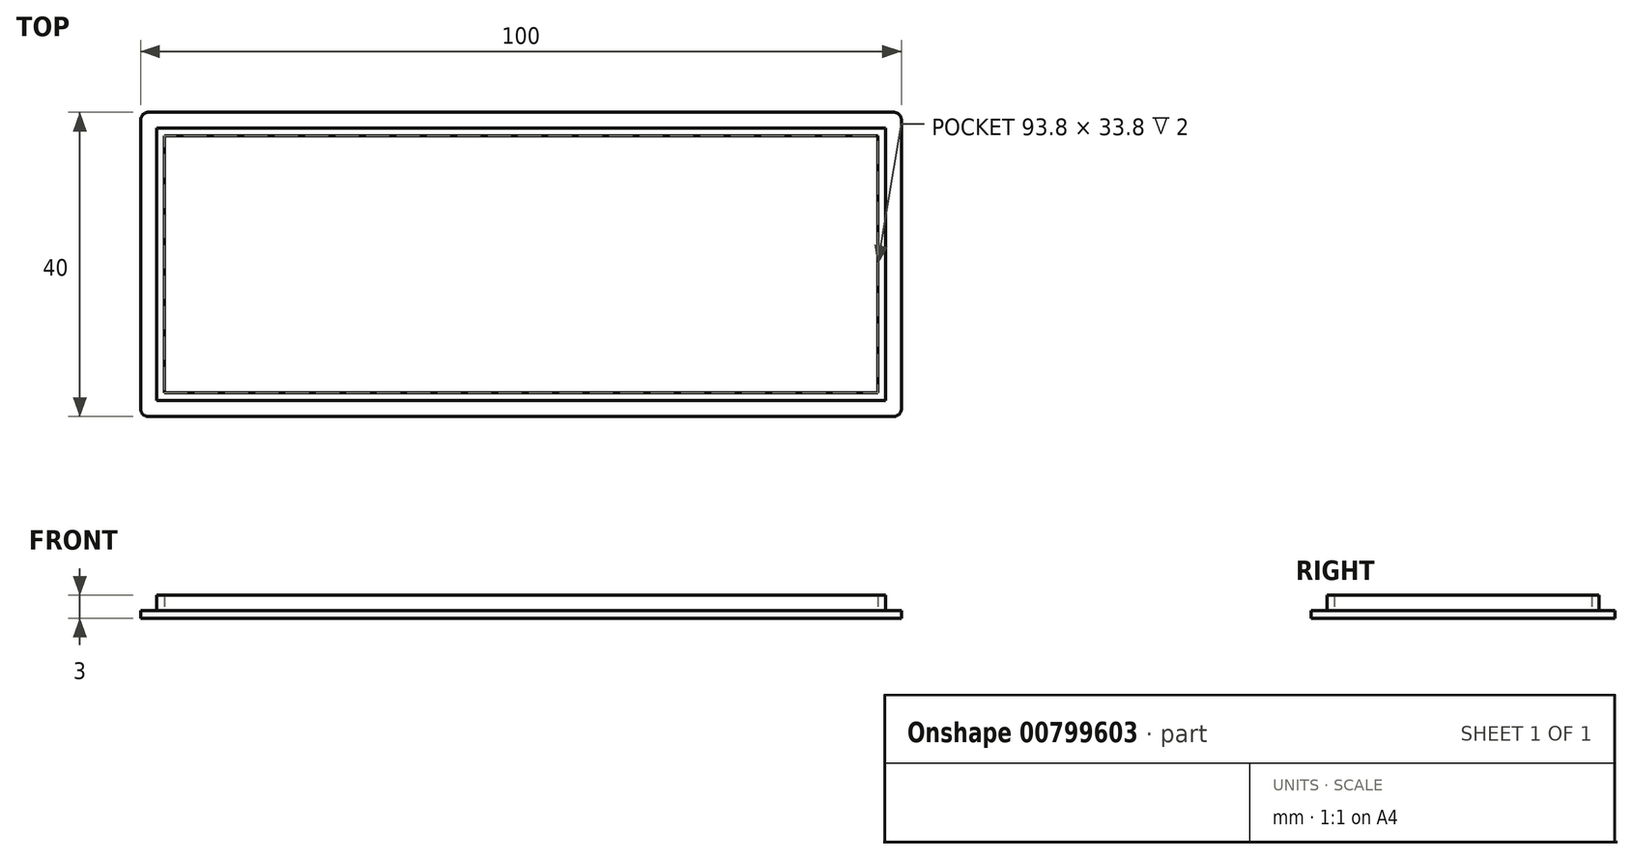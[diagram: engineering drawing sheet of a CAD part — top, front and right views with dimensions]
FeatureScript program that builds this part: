
annotation { "Feature Type Name" : "Feature", "Feature Type Description" : "" }
export const myFeature = defineFeature(function(context is Context, id is Id, definition is map)
    precondition{}
    {
        {
            var Q0;
            Q0=qCreatedBy(makeId("Top.planeOp"),FACE);
            var sketch = newSketch(context, id + "F0", { "sketchPlane" : qUnion([Q0])});
            skLineSegment(sketch, "E0.bottom", {"start": v(0, 0) * mm, "end": v(100, 0) * mm});
            skLineSegment(sketch, "E0.top", {"start": v(0, 40) * mm, "end": v(100, 40) * mm});
            skLineSegment(sketch, "E0.left", {"start": v(0, 0) * mm, "end": v(0, 40) * mm});
            skLineSegment(sketch, "E0.right", {"start": v(100, 0) * mm, "end": v(100, 40) * mm});
            skSolve(sketch);
        }
        {
            var Q0;
            Q0=makeQuery(id+"F0.imprint","IMPRINT",FACE,{"disambiguationData":[TD([[makeQuery(id+"F0.imprint","IMPRINT",EDGE,{"derivedFrom":sQuery(id+"F0.wireOp",EDGE,"E0.bottom")}),1.0]])]});
            extrude(context, id + "F1", {"entities" : qUnion([Q0]), "depth" : 1 * mm, "offsetDistance" : 25 * mm});
        }
        {
            var Q0;
            Q0=makeQuery(id+"F1.opExtrude","CAP_FACE",FACE,{"disambiguationData":[OSD([sQuery(id+"F0.wireOp",EDGE,"E0.bottom"),sQuery(id+"F0.wireOp",EDGE,"E0.top"),sQuery(id+"F0.wireOp",EDGE,"E0.left"),sQuery(id+"F0.wireOp",EDGE,"E0.right")])],"isStart":false});
            var sketch = newSketch(context, id + "F2", { "sketchPlane" : qUnion([Q0])});
            skLineSegment(sketch, "E1.bottom", {"start": v(2.1, 37.9) * mm, "end": v(97.9, 37.9) * mm});
            skLineSegment(sketch, "E1.top", {"start": v(2.1, 2.1) * mm, "end": v(97.9, 2.1) * mm});
            skLineSegment(sketch, "E1.left", {"start": v(2.1, 37.9) * mm, "end": v(2.1, 2.1) * mm});
            skLineSegment(sketch, "E1.right", {"start": v(97.9, 37.9) * mm, "end": v(97.9, 2.1) * mm});
            skLineSegment(sketch, "E2.bottom", {"start": v(3.1, 36.9) * mm, "end": v(96.9, 36.9) * mm});
            skLineSegment(sketch, "E2.top", {"start": v(3.1, 3.1) * mm, "end": v(96.9, 3.1) * mm});
            skLineSegment(sketch, "E2.left", {"start": v(3.1, 36.9) * mm, "end": v(3.1, 3.1) * mm});
            skLineSegment(sketch, "E2.right", {"start": v(96.9, 36.9) * mm, "end": v(96.9, 3.1) * mm});
            skSolve(sketch);
        }
        {
            var Q0;
            Q0=makeQuery(id+"F2.imprint","IMPRINT",FACE,{"disambiguationData":[TD([[makeQuery(id+"F2.imprint","IMPRINT",EDGE,{"derivedFrom":sQuery(id+"F2.wireOp",EDGE,"E1.bottom")}),-1.0]])]});
            extrude(context, id + "F3", {"entities" : qUnion([Q0]), "operationType" : NewBodyOperationType.ADD, "depth" : 2 * mm, "offsetDistance" : 25 * mm});
        }
        {
            var Q0;
            Q0=makeQuery(id+"F1.opExtrude","SWEPT_EDGE",EDGE,{"disambiguationData":[OSD([sQuery(id+"F0.wireOp",EDGE,"E0.bottom"),sQuery(id+"F0.wireOp",EDGE,"E0.left")])]});
            var Q1;
            Q1=makeQuery(id+"F1.opExtrude","SWEPT_EDGE",EDGE,{"disambiguationData":[OSD([sQuery(id+"F0.wireOp",EDGE,"E0.bottom"),sQuery(id+"F0.wireOp",EDGE,"E0.right")])]});
            var Q2;
            Q2=makeQuery(id+"F1.opExtrude","SWEPT_EDGE",EDGE,{"disambiguationData":[OSD([sQuery(id+"F0.wireOp",EDGE,"E0.top"),sQuery(id+"F0.wireOp",EDGE,"E0.right")])]});
            var Q3;
            Q3=makeQuery(id+"F1.opExtrude","SWEPT_EDGE",EDGE,{"disambiguationData":[OSD([sQuery(id+"F0.wireOp",EDGE,"E0.top"),sQuery(id+"F0.wireOp",EDGE,"E0.left")])]});
            fillet(context, id + "F4", {"entities" : qUnion([Q0, Q1, Q2, Q3]), "radius" : 1 * mm, "tangentPropagation" : true, "allowEdgeOverflow" : false});
        }
    });
